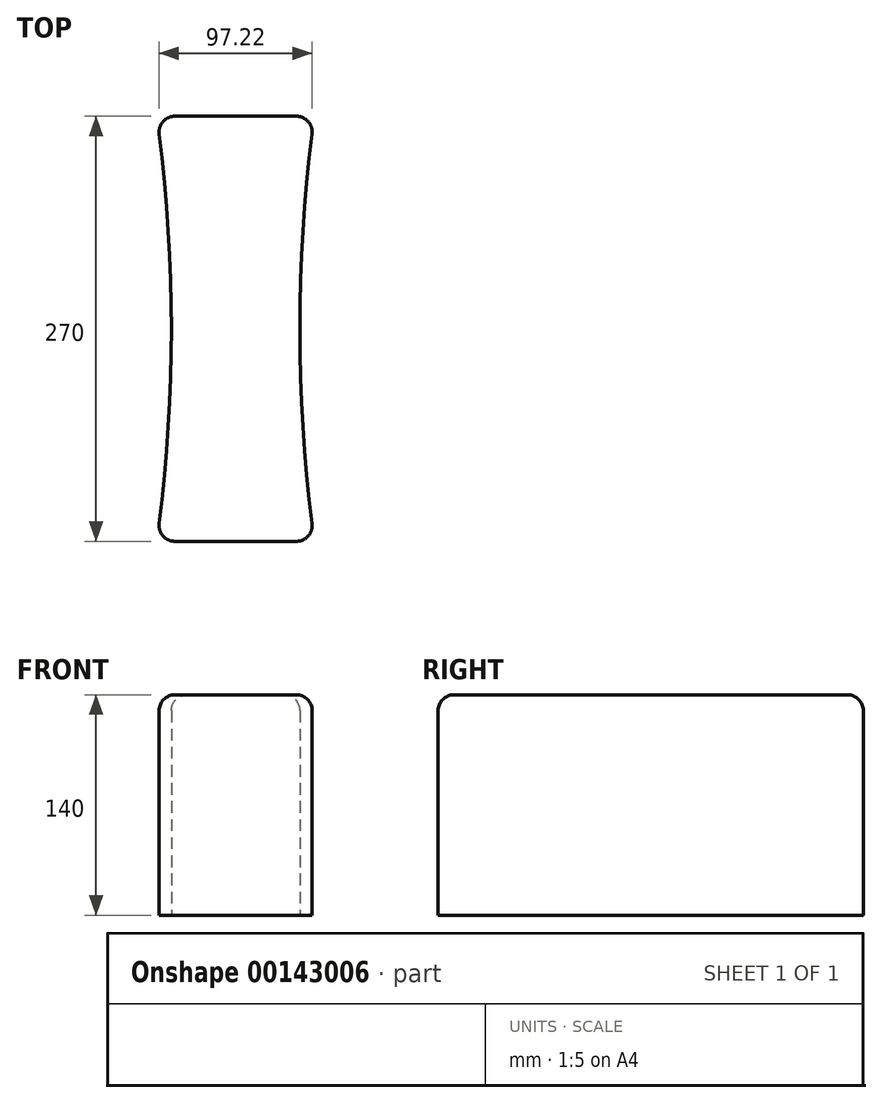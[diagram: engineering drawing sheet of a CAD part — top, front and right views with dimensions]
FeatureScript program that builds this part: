
annotation { "Feature Type Name" : "Feature", "Feature Type Description" : "" }
export const myFeature = defineFeature(function(context is Context, id is Id, definition is map)
    precondition{}
    {
        {
            var Q0;
            Q0=qCreatedBy(makeId("Top.planeOp"),FACE);
            var sketch = newSketch(context, id + "F0", { "sketchPlane" : qUnion([Q0])});
            skLineSegment(sketch, "E0.bottom", {"start": v(11.39, 0) * mm, "end": v(88.61, 0) * mm});
            skLineSegment(sketch, "E0.top", {"start": v(11.39, 270) * mm, "end": v(88.61, 270) * mm});
            skLineSegment(sketch, "E0.left", {"start": v(0, 0) * mm, "end": v(0, 270) * mm, "construction": true});
            skLineSegment(sketch, "E0.right", {"start": v(100, 0) * mm, "end": v(100, 270) * mm, "construction": true});
            skArc(sketch, "E1", {"start": v(98.53, 258.76) * mm, "mid": v(90.85, 135) * mm, "end": v(98.53, 11.24) * mm});
            skLineSegment(sketch, "E2", {"start": v(50, 270) * mm, "end": v(50, 0) * mm, "construction": true});
            skArc(sketch, "E3.MirrorCS", {"start": v(1.47, 258.76) * mm, "mid": v(9.15, 135) * mm, "end": v(1.47, 11.24) * mm});
            skPoint(sketch, "E4.visualSharp", {"position": v(0, 270) * mm});
            skArc(sketch, "E4.filletArc", {"start": v(11.39, 270) * mm, "mid": v(3.9, 266.62) * mm, "end": v(1.47, 258.76) * mm});
            skPoint(sketch, "E5.visualSharp", {"position": v(100, 270) * mm});
            skArc(sketch, "E5.filletArc", {"start": v(98.53, 258.76) * mm, "mid": v(96.1, 266.62) * mm, "end": v(88.61, 270) * mm});
            skPoint(sketch, "E6.visualSharp", {"position": v(100, 0) * mm});
            skArc(sketch, "E6.filletArc", {"start": v(88.61, 0) * mm, "mid": v(96.1, 3.38) * mm, "end": v(98.53, 11.24) * mm});
            skPoint(sketch, "E7.visualSharp", {"position": v(0, 0) * mm});
            skArc(sketch, "E7.filletArc", {"start": v(1.47, 11.24) * mm, "mid": v(3.9, 3.38) * mm, "end": v(11.39, 0) * mm});
            skSolve(sketch);
        }
        {
            var Q0;
            Q0 = qSketchRegion(id + "F0", true);
            extrude(context, id + "F1", {"entities" : qUnion([Q0]), "depth" : 140 * mm});
        }
        {
            var Q0;
            Q0=makeQuery(id+"F1.opExtrude","CAP_FACE",FACE,{"disambiguationData":[OSD([sQuery(id+"F0.wireOp",EDGE,"E0.bottom"),sQuery(id+"F0.wireOp",EDGE,"E0.top"),sQuery(id+"F0.wireOp",EDGE,"E1"),sQuery(id+"F0.wireOp",EDGE,"E3.MirrorCS"),sQuery(id+"F0.wireOp",EDGE,"E4.filletArc"),sQuery(id+"F0.wireOp",EDGE,"E5.filletArc"),sQuery(id+"F0.wireOp",EDGE,"E6.filletArc"),sQuery(id+"F0.wireOp",EDGE,"E7.filletArc")])],"isStart":false});
            fillet(context, id + "F2", {"entities" : qUnion([Q0]), "radius" : 10 * mm, "tangentPropagation" : true, "allowEdgeOverflow" : false});
        }
    });
